# Revit family: Storage-Mounted-Teknion-B_WPL-Wall_Panel_with_Open_Shelves-R2018
name_source: partatom
category: Furniture
revit_build: Autodesk Revit 2018 (Build: 20190510_1515(x64)
units: mm (PartAtom-declared; Revit-internal decimal feet)

## family parameters
Always vertical = Yes
Cut with Voids When Loaded = No
OmniClass Number = 23.40.70.14.64.21
OmniClass Title = Systems Furniture
Room Calculation Point = No
Shared = Yes
Work Plane-Based = No

## types (6) — shared parameters
Assembly Code = E2020200
Light Shelf Finish = Mica - Teknion - V - Satin - Very White
Manufacturer = Teknion
Manufacturer Fax = 416.661.4586
Part Number = B_WPL
Product Documentation Link = http://www.teknion.com
Product Documentation Link #2 = http://www.teknion.com
Product Documentation Link #3 = http://www.teknion.com
Product Documentation Link #4 = http://www.teknion.com
Product Documentation Link #5 = http://www.teknion.com
Product Documentation Link #6 = http://www.teknion.com
Product Documentation Link #7 = http://www.teknion.com
Product Line = Expansion Casegoods
Product Page URL = http://www.teknion.com
Series = Expansion Casegoods
Sustainability Data = http://www.teknion.com
URL = http://www.teknion.com
Unit Weight URL = http://www.teknion.com
Warranty = http://www.teknion.com

## per-type parameters (varying)
| type | 1" Thick Standard Worksurface Mounting Style | 1-3/16" Thick Standard Worksurface Mounting Style | 1-9/16" Thick Standard Worksurface Mounting Style | Bottom of Wall Panel Height | Description | High Secondary Desk Mounting Style | Low Secondary Desk Mounting Style | Model |
| On High Secondary Desk | No | No | No | 26.972 " | Wall Panel with Open Shelves, High Secondary Desk | Yes | No | BHWPL_____ |
| On Low Secondary Desk | No | No | No | 17.425 " | Wall Panel with Open Shelves, Low Secondary Desk | No | Yes | BLWPL_____ |
| On 1" Thick Standard Worksurface | Yes | No | No | 28.823 " | Wall Panel with Open Shelves, On 1" Thick Standard Worksurface | No | No | BDWPL_____ |
| On 1-3/16" Thick Standard Worksurface | No | Yes | No | 28.996 " | Wall Panel with Open Shelves, On 1-3/16" Thick Standard Worksurface | No | No | BMWPL_____ |
| On 1-9/16" Thick Standard Worksurface | No | No | Yes | 29.362 " | Wall Panel with Open Shelves, On 1-9/16" Thick Standard Worksurface | No | No | BXWPL_____ |
| Mid-Height Mounting Style | No | No | No | 21 " | Wall Panel with Open Shelves, Mid-Height Mounting Style | No | No | BKWPL_____ |

type visibility flags (boolean, named after types; folded from table):
- On High Secondary Desk: Yes: (none)
- On Low Secondary Desk: Yes: (none)
- On 1" Thick Standard Worksurface: Yes: (none)
- On 1-3/16" Thick Standard Worksurface: Yes: (none)
- On 1-9/16" Thick Standard Worksurface: Yes: (none)
- Mid-Height Mounting Style: Yes: Mid-Height Mounting Style

## geometry (parser evidence)
native form markers: Sweep x4
no freeform markers — native parametric forms only
